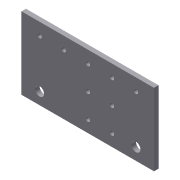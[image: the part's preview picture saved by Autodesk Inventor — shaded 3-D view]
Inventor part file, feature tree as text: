
AUTODESK INVENTOR PART (.ipt)
format: ipt  version: 2012 (Build 160160000, 160)  size: 108,032 bytes
history: native  units: in
note: dims shown in document units (in); Inventor stores cm internally (conversion verified against a paired STEP export)
features: extrude x4, sketch x4, pattern_linear x2
ambient origin geometry x8: Origin, YZ Plane, XZ Plane, XY Plane, X Axis, Y Axis, Z Axis, Center Point
bodies: Solid1 (feature_tree)
feature tree (10):
  extrude  "Extrusion1"  Depth=3.0in
  extrude  "Extrusion2"  Depth=0.5in
  extrude  "Extrusion3"  Depth=4.0in
  pattern_linear  "Rectangular Pattern1"  Spacing1=0.1875in  [1 undecoded]
  extrude  "Extrusion4"  Depth=0.1875in
  pattern_linear  "Rectangular Pattern2"  Spacing1=0.5in  [1 undecoded]
  sketch  "Sketch1"  dims[d0=5.5in d1=3.0in]
  sketch  "Sketch2"  dims[d2=0.1875in d3=0.0in d4=0.5in]
  sketch  "Sketch3"  dims[d5=0.75in d6=4.0in]
  sketch  "Sketch4"  dims[d7=0.375in d8=0.1875in d9=0.0in d10=0.1875in d11=0.5in d13=2.0in d14=0.1875in d15=0.0in d16=0.7874in d18=1.0in d19=0.7874in d21=1.0in d22=0.1875in d23=0.5in d24=0.75in d25=1.0in d26=0.0in d27=1.9685in d29=1.0in]
note: 2 required parameter values undecoded (feature->parameter linkage not recoverable at this tier; creation-order binding heuristic only, values carry confidence <= 0.55)
